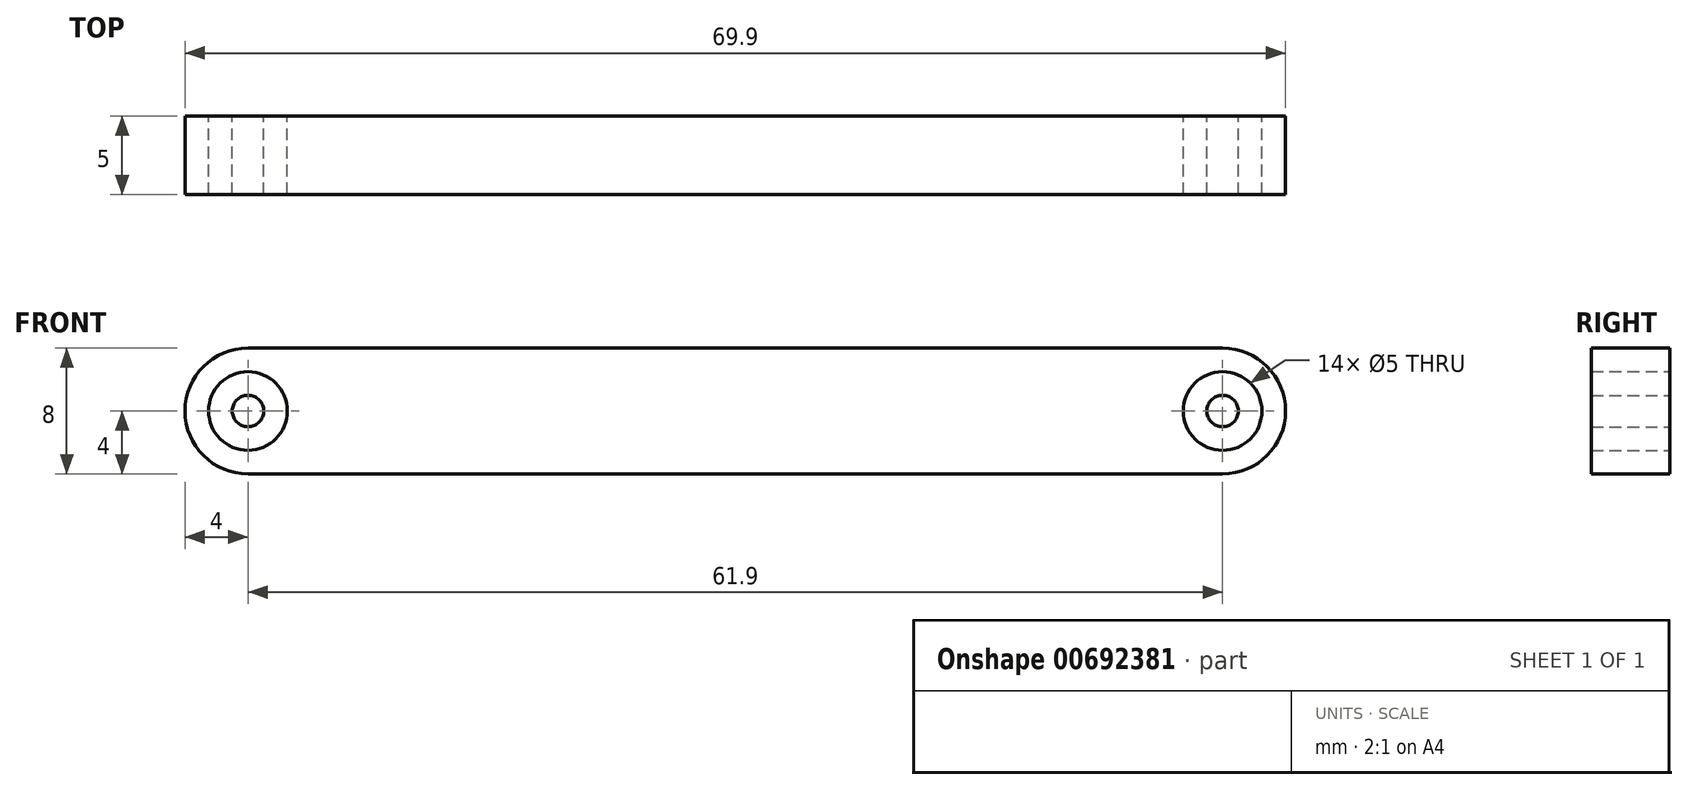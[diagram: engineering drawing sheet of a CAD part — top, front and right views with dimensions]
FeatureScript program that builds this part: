
annotation { "Feature Type Name" : "Feature", "Feature Type Description" : "" }
export const myFeature = defineFeature(function(context is Context, id is Id, definition is map)
    precondition{}
    {
        {
            var Q0;
            Q0=qCreatedBy(makeId("Front.planeOp"),FACE);
            var sketch = newSketch(context, id + "F0", { "sketchPlane" : qUnion([Q0])});
            skArc(sketch, "E0", {"start": v(0, 4) * mm, "mid": v(-4, 0) * mm, "end": v(0, -4) * mm});
            skArc(sketch, "E1", {"start": v(61.9, -4) * mm, "mid": v(65.9, 0) * mm, "end": v(61.9, 4) * mm});
            skLineSegment(sketch, "E2", {"start": v(0, 4) * mm, "end": v(61.9, 4) * mm});
            skLineSegment(sketch, "E3", {"start": v(0, -4) * mm, "end": v(61.9, -4) * mm});
            skCircle(sketch, "E4", {"center": v(0, 0) * mm, "radius": 2.5 * mm});
            skCircle(sketch, "E5", {"center": v(0, 0) * mm, "radius": 1 * mm});
            skCircle(sketch, "E6", {"center": v(61.9, 0) * mm, "radius": 2.5 * mm});
            skCircle(sketch, "E7", {"center": v(61.9, 0) * mm, "radius": 1 * mm});
            skSolve(sketch);
        }
        {
            var Q0;
            Q0 = qSketchRegion(id + "F0", true);
            var Q1;
            Q1=makeQuery(id+"F0.imprint","IMPRINT",FACE,{"disambiguationData":[TD([[makeQuery(id+"F0.imprint","IMPRINT",EDGE,{"derivedFrom":sQuery(id+"F0.wireOp",EDGE,"E5")}),1.0]])]});
            var Q2;
            Q2=makeQuery(id+"F0.imprint","IMPRINT",FACE,{"disambiguationData":[TD([[makeQuery(id+"F0.imprint","IMPRINT",EDGE,{"derivedFrom":sQuery(id+"F0.wireOp",EDGE,"E7")}),1.0]])]});
            extrude(context, id + "F1", {"entities" : qUnion([Q0, Q1, Q2]), "depth" : 5 * mm, "offsetDistance" : 25 * mm});
        }
    });
